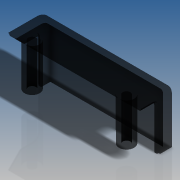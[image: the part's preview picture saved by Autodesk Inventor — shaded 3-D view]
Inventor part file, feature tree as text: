
AUTODESK INVENTOR PART (.ipt)
format: ipt  version: 2016 SP2 (Build 200236200, 236)  size: 268,800 bytes
history: native  units: in
note: dims shown in document units (in); Inventor stores cm internally (conversion verified against a paired STEP export)
features: extrude x4, sketch x3, plane x1, mirror x1, fillet x1
ambient origin geometry x8: Origin, YZ Plane, XZ Plane, XY Plane, X Axis, Y Axis, Z Axis, Center Point
bodies: Solid1 (feature_tree)
feature tree (10):
  sketch  "Sketch2"  dims[d0=0.1417in d1=0.0472in]
  extrude  "Extrusion1"  Depth=0.0472in
  extrude  "Extrusion2"  Depth=0.0472in
  plane  "Work Plane1"
  extrude  "Extrusion3"  Depth=0.0039in
  extrude  "Extrusion4"  Depth=0.0039in
  mirror  "Mirror1"
  fillet  "Fillet1"  Radius=0.1417in
  sketch  "Sketch3"  dims[d2=45.0deg d3=0.0472in]
  sketch  "Sketch4"  dims[d4=0.1417in d5=0.6142in d6=0.0157in d7=0.1417in d9=0.4409in d10=1.2598in d11=0.0in d12=1.1654in d13=0.0in d14=0.4409in d15=0.9764in d16=0.1575in d17=0.0787in d18=0.2835in d19=1.1654in d20=0.0in d21=0.0157in d22=0.0157in d23=0.0in d24=0.0039in]
